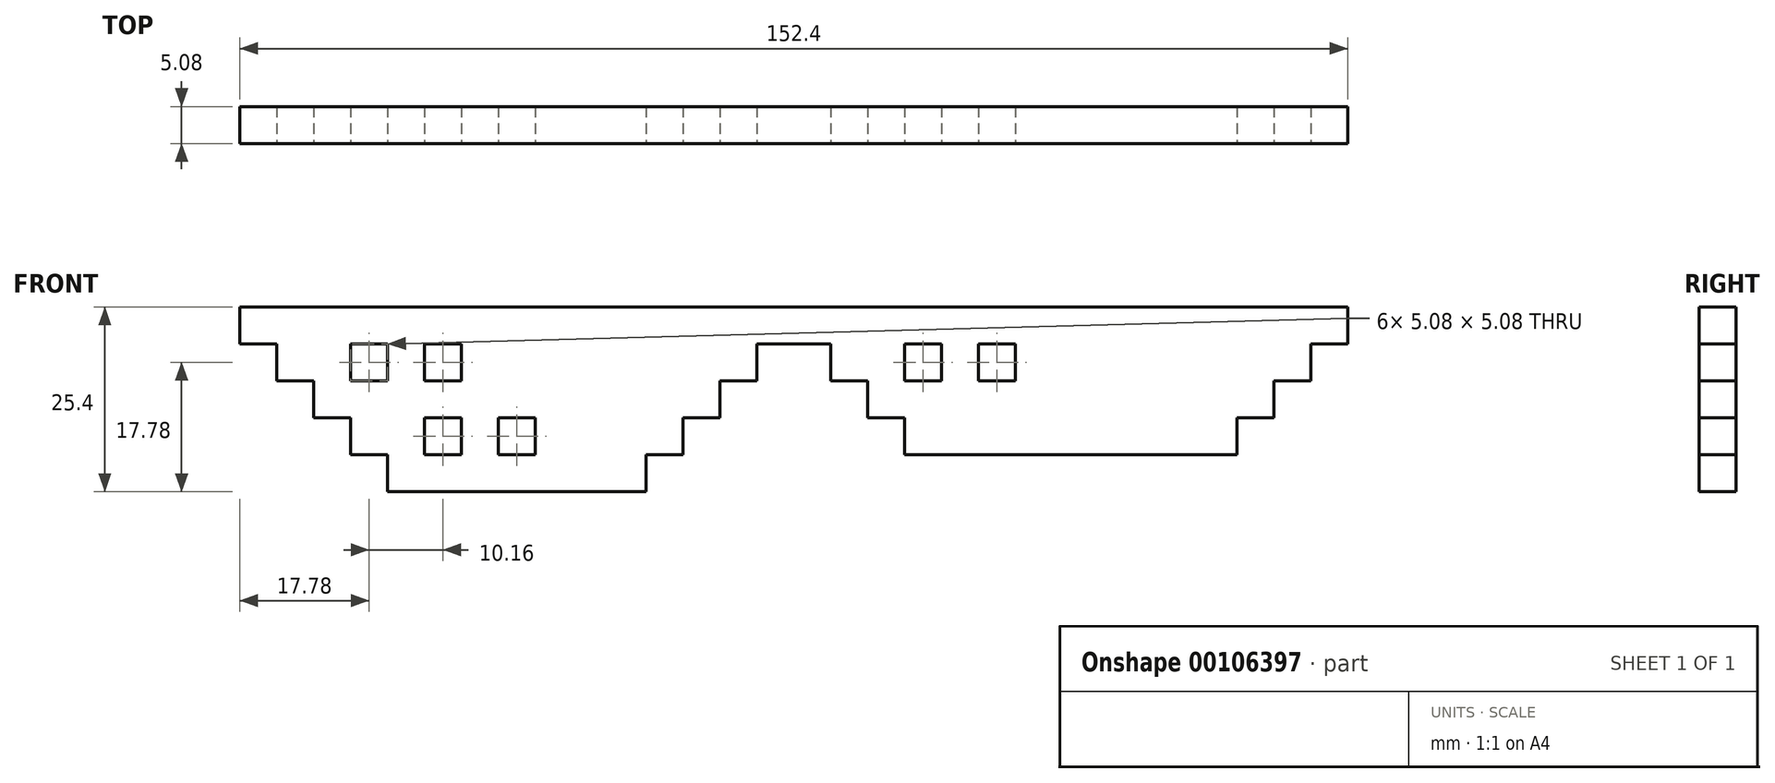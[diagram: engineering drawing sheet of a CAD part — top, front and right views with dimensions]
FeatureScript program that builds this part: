
annotation { "Feature Type Name" : "Feature", "Feature Type Description" : "" }
export const myFeature = defineFeature(function(context is Context, id is Id, definition is map)
    precondition{}
    {
        {
            var Q0;
            Q0=qCreatedBy(makeId("Front.planeOp"),FACE);
            var sketch = newSketch(context, id + "F0", { "sketchPlane" : qUnion([Q0])});
            skLineSegment(sketch, "E0", {"start": v(0, 10.16) * mm, "end": v(-76.2, 10.16) * mm});
            skLineSegment(sketch, "E1", {"start": v(-76.2, 10.16) * mm, "end": v(-76.2, 5.08) * mm});
            skLineSegment(sketch, "E2", {"start": v(-76.2, 5.08) * mm, "end": v(-71.12, 5.08) * mm});
            skLineSegment(sketch, "E3", {"start": v(-71.12, 5.08) * mm, "end": v(-71.12, 0) * mm});
            skLineSegment(sketch, "E4", {"start": v(-71.12, 0) * mm, "end": v(-66.04, 0) * mm});
            skLineSegment(sketch, "E5", {"start": v(-66.04, 0) * mm, "end": v(-66.04, -5.08) * mm});
            skLineSegment(sketch, "E6", {"start": v(-66.04, -5.08) * mm, "end": v(-60.96, -5.08) * mm});
            skLineSegment(sketch, "E7", {"start": v(-60.96, -5.08) * mm, "end": v(-60.96, -10.16) * mm});
            skLineSegment(sketch, "E8", {"start": v(-60.96, -10.16) * mm, "end": v(-55.88, -10.16) * mm});
            skLineSegment(sketch, "E9", {"start": v(-55.88, -10.16) * mm, "end": v(-55.88, -15.24) * mm});
            skLineSegment(sketch, "E10", {"start": v(0, 10.16) * mm, "end": v(0, 5.08) * mm});
            skLineSegment(sketch, "E11", {"start": v(0, 5.08) * mm, "end": v(-5.08, 5.08) * mm});
            skLineSegment(sketch, "E12", {"start": v(-5.08, 5.08) * mm, "end": v(-5.08, 0) * mm});
            skLineSegment(sketch, "E13", {"start": v(-5.08, 0) * mm, "end": v(-10.16, 0) * mm});
            skLineSegment(sketch, "E14", {"start": v(-10.16, 0) * mm, "end": v(-10.16, -5.08) * mm});
            skLineSegment(sketch, "E15", {"start": v(-10.16, -5.08) * mm, "end": v(-15.24, -5.08) * mm});
            skLineSegment(sketch, "E16", {"start": v(-15.24, -5.08) * mm, "end": v(-15.24, -10.16) * mm});
            skLineSegment(sketch, "E17", {"start": v(-15.24, -10.16) * mm, "end": v(-20.32, -10.16) * mm});
            skLineSegment(sketch, "E18", {"start": v(-20.32, -10.16) * mm, "end": v(-20.32, -15.24) * mm});
            skLineSegment(sketch, "E19", {"start": v(-55.88, -15.24) * mm, "end": v(-20.32, -15.24) * mm});
            skLineSegment(sketch, "E20.MirrorCS", {"start": v(60.96, -10.16) * mm, "end": v(55.88, -10.16) * mm});
            skLineSegment(sketch, "E21.MirrorCS", {"start": v(66.04, -5.08) * mm, "end": v(60.96, -5.08) * mm});
            skLineSegment(sketch, "E22.MirrorCS", {"start": v(15.24, -10.16) * mm, "end": v(20.32, -10.16) * mm});
            skLineSegment(sketch, "E23.MirrorCS", {"start": v(76.2, 10.16) * mm, "end": v(76.2, 5.08) * mm});
            skLineSegment(sketch, "E24.MirrorCS", {"start": v(66.04, 0) * mm, "end": v(66.04, -5.08) * mm});
            skLineSegment(sketch, "E25.MirrorCS", {"start": v(10.16, -5.08) * mm, "end": v(15.24, -5.08) * mm});
            skLineSegment(sketch, "E26.MirrorCS", {"start": v(76.2, 5.08) * mm, "end": v(71.12, 5.08) * mm});
            skLineSegment(sketch, "E27.MirrorCS", {"start": v(5.08, 0) * mm, "end": v(10.16, 0) * mm});
            skLineSegment(sketch, "E28.MirrorCS", {"start": v(15.24, -5.08) * mm, "end": v(15.24, -10.16) * mm});
            skLineSegment(sketch, "E29.MirrorCS", {"start": v(71.12, 5.08) * mm, "end": v(71.12, 0) * mm});
            skLineSegment(sketch, "E30.MirrorCS", {"start": v(0, 10.16) * mm, "end": v(76.2, 10.16) * mm});
            skLineSegment(sketch, "E31.MirrorCS", {"start": v(10.16, 0) * mm, "end": v(10.16, -5.08) * mm});
            skLineSegment(sketch, "E32.MirrorCS", {"start": v(60.96, -5.08) * mm, "end": v(60.96, -10.16) * mm});
            skLineSegment(sketch, "E33.MirrorCS", {"start": v(71.12, 0) * mm, "end": v(66.04, 0) * mm});
            skLineSegment(sketch, "E34.MirrorCS", {"start": v(5.08, 5.08) * mm, "end": v(5.08, 0) * mm});
            skLineSegment(sketch, "E35.MirrorCS", {"start": v(0, 5.08) * mm, "end": v(5.08, 5.08) * mm});
            skLineSegment(sketch, "E36", {"start": v(20.32, -10.16) * mm, "end": v(55.88, -10.16) * mm});
            skLineSegment(sketch, "E37.bottom", {"start": v(-60.96, 5.08) * mm, "end": v(-55.88, 5.08) * mm});
            skLineSegment(sketch, "E37.top", {"start": v(-60.96, 0) * mm, "end": v(-55.88, 0) * mm});
            skLineSegment(sketch, "E37.left", {"start": v(-60.96, 5.08) * mm, "end": v(-60.96, 0) * mm});
            skLineSegment(sketch, "E37.right", {"start": v(-55.88, 5.08) * mm, "end": v(-55.88, 0) * mm});
            skLineSegment(sketch, "E38.bottom", {"start": v(-50.8, -5.08) * mm, "end": v(-45.72, -5.08) * mm});
            skLineSegment(sketch, "E38.top", {"start": v(-50.8, -10.16) * mm, "end": v(-45.72, -10.16) * mm});
            skLineSegment(sketch, "E38.left", {"start": v(-50.8, -5.08) * mm, "end": v(-50.8, -10.16) * mm});
            skLineSegment(sketch, "E38.right", {"start": v(-45.72, -5.08) * mm, "end": v(-45.72, -10.16) * mm});
            skLineSegment(sketch, "E39.bottom", {"start": v(-50.8, 5.08) * mm, "end": v(-45.72, 5.08) * mm});
            skLineSegment(sketch, "E39.top", {"start": v(-50.8, 0) * mm, "end": v(-45.72, 0) * mm});
            skLineSegment(sketch, "E39.left", {"start": v(-50.8, 5.08) * mm, "end": v(-50.8, 0) * mm});
            skLineSegment(sketch, "E39.right", {"start": v(-45.72, 5.08) * mm, "end": v(-45.72, 0) * mm});
            skLineSegment(sketch, "E40.bottom", {"start": v(-40.64, -5.08) * mm, "end": v(-35.56, -5.08) * mm});
            skLineSegment(sketch, "E40.top", {"start": v(-40.64, -10.16) * mm, "end": v(-35.56, -10.16) * mm});
            skLineSegment(sketch, "E40.left", {"start": v(-40.64, -5.08) * mm, "end": v(-40.64, -10.16) * mm});
            skLineSegment(sketch, "E40.right", {"start": v(-35.56, -5.08) * mm, "end": v(-35.56, -10.16) * mm});
            skLineSegment(sketch, "E41.bottom", {"start": v(15.24, 5.08) * mm, "end": v(20.32, 5.08) * mm});
            skLineSegment(sketch, "E41.top", {"start": v(15.24, 0) * mm, "end": v(20.32, 0) * mm});
            skLineSegment(sketch, "E41.left", {"start": v(15.24, 5.08) * mm, "end": v(15.24, 0) * mm});
            skLineSegment(sketch, "E41.right", {"start": v(20.32, 5.08) * mm, "end": v(20.32, 0) * mm});
            skLineSegment(sketch, "E42.top", {"start": v(20.32, -5.08) * mm, "end": v(25.4, -5.08) * mm});
            skLineSegment(sketch, "E43.bottom", {"start": v(25.4, 0) * mm, "end": v(30.48, 0) * mm});
            skLineSegment(sketch, "E43.top", {"start": v(25.4, 5.08) * mm, "end": v(30.48, 5.08) * mm});
            skLineSegment(sketch, "E43.left", {"start": v(25.4, 0) * mm, "end": v(25.4, 5.08) * mm});
            skLineSegment(sketch, "E43.right", {"start": v(30.48, 0) * mm, "end": v(30.48, 5.08) * mm});
            skLineSegment(sketch, "E44.top", {"start": v(30.48, -5.08) * mm, "end": v(35.56, -5.08) * mm});
            skLineSegment(sketch, "E45.bottom", {"start": v(-50.8, -5.08) * mm, "end": v(-55.88, -5.08) * mm});
            skLineSegment(sketch, "E45.top", {"start": v(-50.8, 0) * mm, "end": v(-55.88, 0) * mm});
            skLineSegment(sketch, "E46.bottom", {"start": v(-45.72, 0) * mm, "end": v(-40.64, 0) * mm});
            skLineSegment(sketch, "E46.top", {"start": v(-45.72, -5.08) * mm, "end": v(-40.64, -5.08) * mm});
            skSolve(sketch);
        }
        {
            var Q0;
            Q0=makeQuery(id+"F0.imprint","IMPRINT",FACE,{"disambiguationData":[TD([[makeQuery(id+"F0.imprint","IMPRINT",EDGE,{"derivedFrom":sQuery(id+"F0.wireOp",EDGE,"E9uyCXlz-XDpy-Z0D1-HOVF-rQak1OJCefLN.bottom")}),-1.0]])]});
            var Q1;
            Q1=makeQuery(id+"F0.imprint","IMPRINT",FACE,{"disambiguationData":[TD([[makeQuery(id+"F0.imprint","IMPRINT",EDGE,{"derivedFrom":sQuery(id+"F0.wireOp",EDGE,"BF7fgjOQ-s8u8-rG3K-cKgi-U6GtlgQVvfko.bottom")}),-1.0]])]});
            var Q2;
            Q2=makeQuery(id+"F0.imprint","IMPRINT",FACE,{"disambiguationData":[TD([[makeQuery(id+"F0.imprint","IMPRINT",EDGE,{"derivedFrom":sQuery(id+"F0.wireOp",EDGE,"E42.bottom")}),-1.0]])]});
            var Q3;
            Q3=makeQuery(id+"F0.imprint","IMPRINT",FACE,{"disambiguationData":[TD([[makeQuery(id+"F0.imprint","IMPRINT",EDGE,{"derivedFrom":sQuery(id+"F0.wireOp",EDGE,"E44.bottom")}),-1.0]])]});
            var Q4;
            Q4=makeQuery(id+"F0.imprint","IMPRINT",FACE,{"disambiguationData":[TD([[makeQuery(id+"F0.imprint","IMPRINT",EDGE,{"derivedFrom":sQuery(id+"F0.wireOp",EDGE,"E0")}),1.0]])]});
            var Q5;
            Q5=makeQuery(id+"F0.imprint","IMPRINT",FACE,{"disambiguationData":[TD([[makeQuery(id+"F0.imprint","IMPRINT",EDGE,{"derivedFrom":sQuery(id+"F0.wireOp",EDGE,"E10")}),1.0]])]});
            var Q6;
            Q6=makeQuery(id+"F0.imprint","IMPRINT",FACE,{"disambiguationData":[TD([[makeQuery(id+"F0.imprint","IMPRINT",EDGE,{"derivedFrom":sQuery(id+"F0.wireOp",EDGE,"BF7fgjOQ-s8u8-rG3K-cKgi-U6GtlgQVvfko.right")}),1.0]])]});
            var Q7;
            Q7=makeQuery(id+"F0.imprint","IMPRINT",FACE,{"disambiguationData":[TD([[makeQuery(id+"F0.imprint","IMPRINT",EDGE,{"derivedFrom":sQuery(id+"F0.wireOp",EDGE,"E38.bottom")}),1.0]])]});
            extrude(context, id + "F1", {"entities" : qUnion([Q0, Q1, Q2, Q3, Q4, Q5, Q6, Q7]), "oppositeDirection" : true, "depth" : 5.08 * mm});
        }
    });
